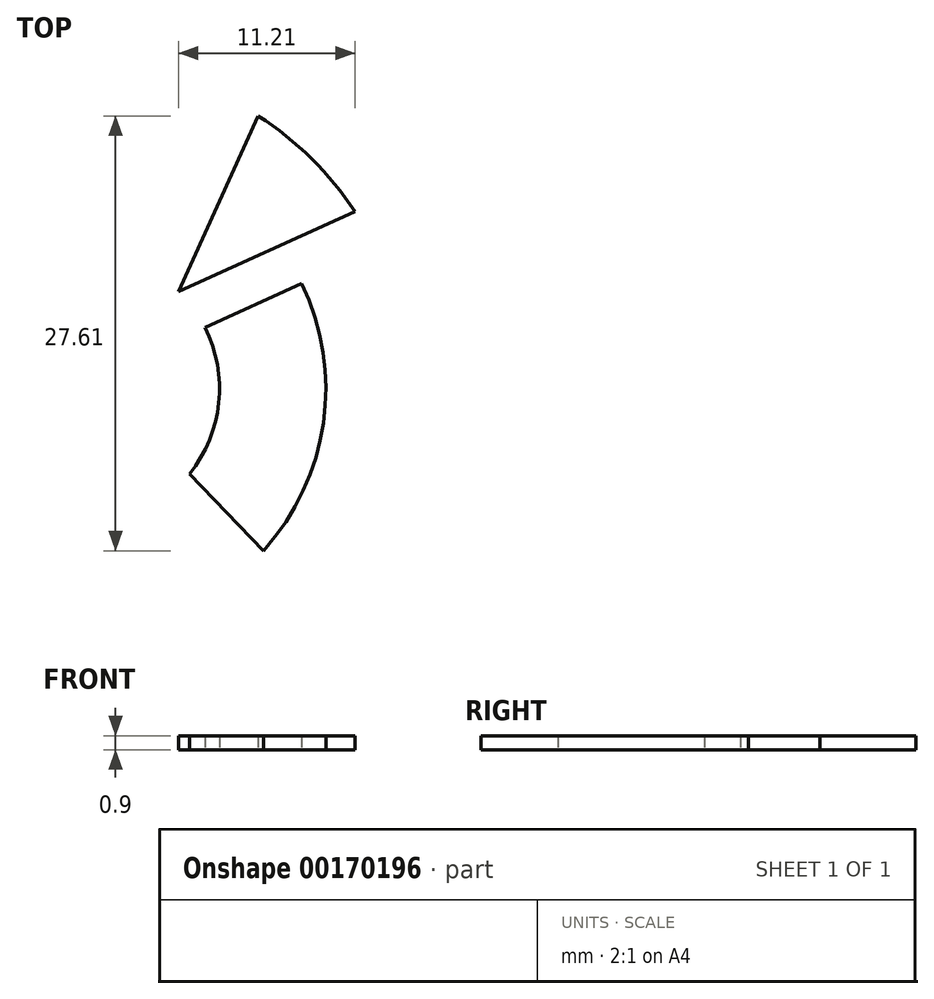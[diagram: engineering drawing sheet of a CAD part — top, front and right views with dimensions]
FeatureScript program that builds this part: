
annotation { "Feature Type Name" : "Feature", "Feature Type Description" : "" }
export const myFeature = defineFeature(function(context is Context, id is Id, definition is map)
    precondition{}
    {
        {
            var Q0;
            Q0=qCreatedBy(makeId("Top.planeOp"),FACE);
            var sketch = newSketch(context, id + "F0", { "sketchPlane" : qUnion([Q0])});
            skCircle(sketch, "E0", {"center": v(0, 0) * mm, "radius": 20 * mm});
            skCircle(sketch, "E1", {"center": v(0, 0) * mm, "radius": 13.35 * mm});
            skCircle(sketch, "E2", {"center": v(0, 0) * mm, "radius": 4.06 * mm});
            skCircle(sketch, "E3", {"center": v(0, 0) * mm, "radius": 10.58 * mm});
            skCircle(sketch, "E4", {"center": v(0, 0) * mm, "radius": 8.61 * mm});
            skCircle(sketch, "E5", {"center": v(0, 0) * mm, "radius": 15.36 * mm});
            skCircle(sketch, "E6", {"center": v(0, 0) * mm, "radius": 20.56 * mm});
            skCircle(sketch, "E7", {"center": v(0, 21.5) * mm, "radius": 3.37 * mm});
            skCircle(sketch, "E8", {"center": v(0, 22.43) * mm, "radius": 1.5 * mm});
            skLineSegment(sketch, "E9", {"start": v(6, 6.18) * mm, "end": v(11.07, 17.32) * mm});
            skLineSegment(sketch, "E10", {"start": v(6, 6.18) * mm, "end": v(17.22, 11.24) * mm});
            skLineSegment(sketch, "E11", {"start": v(8.19, 18.25) * mm, "end": v(1.98, 3.54) * mm});
            skLineSegment(sketch, "E12", {"start": v(1.66, -3.7) * mm, "end": v(12.41, -15.68) * mm});
            skLineSegment(sketch, "E13", {"start": v(7.68, 3.9) * mm, "end": v(13.83, 6.68) * mm});
            skLineSegment(sketch, "E14", {"start": v(11.4, -10.3) * mm, "end": v(6.71, -5.4) * mm});
            skSolve(sketch);
        }
        {
            var Q0;
            {var subQ1=sQuery(id+"F0.wireOp",EDGE,"E0");var subQ4=sQuery(id+"F0.wireOp",EDGE,"E11");var subQ10=makeQuery(id+"F0.imprint","INTERSECT",VERTEX,{"derivedFrom":[subQ1,subQ4]});Q0=makeQuery(id+"F0.imprint","IMPRINT",FACE,{"disambiguationData":[TD([[makeQuery(id+"F0.imprint","IMPRINT",EDGE,{"disambiguationData":[TD([[subQ10,-1.0]])],"derivedFrom":subQ1}),1.0]])]});}
            var Q1;
            {var subQ0=sQuery(id+"F0.wireOp",EDGE,"E11");var subQ1=sQuery(id+"F0.wireOp",EDGE,"E1");var subQ2=makeQuery(id+"F0.imprint","INTERSECT",VERTEX,{"derivedFrom":[subQ1,subQ0]});Q1=makeQuery(id+"F0.imprint","IMPRINT",FACE,{"disambiguationData":[TD([[makeQuery(id+"F0.imprint","IMPRINT",EDGE,{"disambiguationData":[TD([[subQ2,-1.0]])],"derivedFrom":subQ1}),-1.0]])]});}
            var Q2;
            {var subQ0=sQuery(id+"F0.wireOp",EDGE,"E11");var subQ1=sQuery(id+"F0.wireOp",EDGE,"E1");var subQ2=makeQuery(id+"F0.imprint","INTERSECT",VERTEX,{"derivedFrom":[subQ1,subQ0]});Q2=makeQuery(id+"F0.imprint","IMPRINT",FACE,{"disambiguationData":[TD([[makeQuery(id+"F0.imprint","IMPRINT",EDGE,{"disambiguationData":[TD([[subQ2,-1.0]])],"derivedFrom":subQ1}),1.0]])]});}
            var Q3;
            {var subQ0=sQuery(id+"F0.wireOp",EDGE,"E11");var subQ1=sQuery(id+"F0.wireOp",EDGE,"E3");var subQ2=makeQuery(id+"F0.imprint","INTERSECT",VERTEX,{"derivedFrom":[subQ1,subQ0]});Q3=makeQuery(id+"F0.imprint","IMPRINT",FACE,{"disambiguationData":[TD([[makeQuery(id+"F0.imprint","IMPRINT",EDGE,{"disambiguationData":[TD([[subQ2,-1.0]])],"derivedFrom":subQ1}),1.0]])]});}
            var Q4;
            {var subQ0=sQuery(id+"F0.wireOp",EDGE,"E11");var subQ1=sQuery(id+"F0.wireOp",EDGE,"E2");var subQ2=makeQuery(id+"F0.imprint","INTERSECT",VERTEX,{"derivedFrom":[subQ1,subQ0]});Q4=makeQuery(id+"F0.imprint","IMPRINT",FACE,{"disambiguationData":[TD([[makeQuery(id+"F0.imprint","IMPRINT",EDGE,{"disambiguationData":[TD([[subQ2,-1.0]])],"derivedFrom":subQ1}),-1.0]])]});}
            var Q5;
            {var subQ0=sQuery(id+"F0.wireOp",EDGE,"E7");var subQ1=sQuery(id+"F0.wireOp",EDGE,"E0");var subQ2=makeQuery(id+"F0.imprint","INTERSECT",VERTEX,{"disambiguationData":[OD(0.0)],"derivedFrom":[subQ1,subQ0]});Q5=makeQuery(id+"F0.imprint","IMPRINT",FACE,{"disambiguationData":[TD([[makeQuery(id+"F0.imprint","IMPRINT",EDGE,{"disambiguationData":[TD([[subQ2,-1.0]])],"derivedFrom":subQ1}),1.0]])]});}
            var Q6;
            {var subQ0=sQuery(id+"F0.wireOp",EDGE,"E7");var subQ1=sQuery(id+"F0.wireOp",EDGE,"E0");var subQ2=makeQuery(id+"F0.imprint","INTERSECT",VERTEX,{"disambiguationData":[OD(0.0)],"derivedFrom":[subQ1,subQ0]});Q6=makeQuery(id+"F0.imprint","IMPRINT",FACE,{"disambiguationData":[TD([[makeQuery(id+"F0.imprint","IMPRINT",EDGE,{"disambiguationData":[TD([[subQ2,-1.0]])],"derivedFrom":subQ1}),-1.0]])]});}
            var Q7;
            Q7=makeQuery(id+"F0.imprint","IMPRINT",FACE,{"disambiguationData":[TD([[makeQuery(id+"F0.imprint","IMPRINT",EDGE,{"derivedFrom":sQuery(id+"F0.wireOp",EDGE,"E8")}),-1.0]])]});
            var Q8;
            {var subQ0=sQuery(id+"F0.wireOp",EDGE,"E10");var subQ1=sQuery(id+"F0.wireOp",EDGE,"E1");var subQ2=makeQuery(id+"F0.imprint","INTERSECT",VERTEX,{"derivedFrom":[subQ1,subQ0]});Q8=makeQuery(id+"F0.imprint","IMPRINT",FACE,{"disambiguationData":[TD([[makeQuery(id+"F0.imprint","IMPRINT",EDGE,{"disambiguationData":[TD([[subQ2,1.0]])],"derivedFrom":subQ1}),-1.0]])]});}
            var Q9;
            {var subQ0=sQuery(id+"F0.wireOp",EDGE,"E10");var subQ1=sQuery(id+"F0.wireOp",EDGE,"E1");var subQ2=makeQuery(id+"F0.imprint","INTERSECT",VERTEX,{"derivedFrom":[subQ1,subQ0]});Q9=makeQuery(id+"F0.imprint","IMPRINT",FACE,{"disambiguationData":[TD([[makeQuery(id+"F0.imprint","IMPRINT",EDGE,{"disambiguationData":[TD([[subQ2,1.0]])],"derivedFrom":subQ1}),1.0]])]});}
            var Q10;
            {var subQ0=sQuery(id+"F0.wireOp",EDGE,"E10");var subQ1=sQuery(id+"F0.wireOp",EDGE,"E3");var subQ2=makeQuery(id+"F0.imprint","INTERSECT",VERTEX,{"derivedFrom":[subQ1,subQ0]});Q10=makeQuery(id+"F0.imprint","IMPRINT",FACE,{"disambiguationData":[TD([[makeQuery(id+"F0.imprint","IMPRINT",EDGE,{"disambiguationData":[TD([[subQ2,1.0]])],"derivedFrom":subQ1}),1.0]])]});}
            var Q11;
            {var subQ0=sQuery(id+"F0.wireOp",EDGE,"E9");var subQ1=sQuery(id+"F0.wireOp",EDGE,"E3");var subQ2=makeQuery(id+"F0.imprint","INTERSECT",VERTEX,{"derivedFrom":[subQ1,subQ0]});Q11=makeQuery(id+"F0.imprint","IMPRINT",FACE,{"disambiguationData":[TD([[makeQuery(id+"F0.imprint","IMPRINT",EDGE,{"disambiguationData":[TD([[subQ2,1.0]])],"derivedFrom":subQ1}),1.0]])]});}
            var Q12;
            {var subQ0=sQuery(id+"F0.wireOp",EDGE,"E9");var subQ1=sQuery(id+"F0.wireOp",EDGE,"E3");var subQ2=makeQuery(id+"F0.imprint","INTERSECT",VERTEX,{"derivedFrom":[subQ1,subQ0]});Q12=makeQuery(id+"F0.imprint","IMPRINT",FACE,{"disambiguationData":[TD([[makeQuery(id+"F0.imprint","IMPRINT",EDGE,{"disambiguationData":[TD([[subQ2,-1.0]])],"derivedFrom":subQ1}),1.0]])]});}
            var Q13;
            {var subQ0=sQuery(id+"F0.wireOp",EDGE,"E9");var subQ1=sQuery(id+"F0.wireOp",EDGE,"E1");var subQ2=makeQuery(id+"F0.imprint","INTERSECT",VERTEX,{"derivedFrom":[subQ1,subQ0]});Q13=makeQuery(id+"F0.imprint","IMPRINT",FACE,{"disambiguationData":[TD([[makeQuery(id+"F0.imprint","IMPRINT",EDGE,{"disambiguationData":[TD([[subQ2,-1.0]])],"derivedFrom":subQ1}),1.0]])]});}
            var Q14;
            {var subQ0=sQuery(id+"F0.wireOp",EDGE,"E9");var subQ1=sQuery(id+"F0.wireOp",EDGE,"E1");var subQ2=makeQuery(id+"F0.imprint","INTERSECT",VERTEX,{"derivedFrom":[subQ1,subQ0]});Q14=makeQuery(id+"F0.imprint","IMPRINT",FACE,{"disambiguationData":[TD([[makeQuery(id+"F0.imprint","IMPRINT",EDGE,{"disambiguationData":[TD([[subQ2,-1.0]])],"derivedFrom":subQ1}),-1.0]])]});}
            var Q15;
            {var subQ0=sQuery(id+"F0.wireOp",EDGE,"E9");var subQ1=sQuery(id+"F0.wireOp",EDGE,"E1");var subQ2=makeQuery(id+"F0.imprint","INTERSECT",VERTEX,{"derivedFrom":[subQ1,subQ0]});Q15=makeQuery(id+"F0.imprint","IMPRINT",FACE,{"disambiguationData":[TD([[makeQuery(id+"F0.imprint","IMPRINT",EDGE,{"disambiguationData":[TD([[subQ2,1.0]])],"derivedFrom":subQ1}),1.0]])]});}
            var Q16;
            {var subQ0=sQuery(id+"F0.wireOp",EDGE,"E9");var subQ1=sQuery(id+"F0.wireOp",EDGE,"E1");var subQ2=makeQuery(id+"F0.imprint","INTERSECT",VERTEX,{"derivedFrom":[subQ1,subQ0]});Q16=makeQuery(id+"F0.imprint","IMPRINT",FACE,{"disambiguationData":[TD([[makeQuery(id+"F0.imprint","IMPRINT",EDGE,{"disambiguationData":[TD([[subQ2,1.0]])],"derivedFrom":subQ1}),-1.0]])]});}
            var Q17;
            {var subQ0=sQuery(id+"F0.wireOp",EDGE,"E9");var subQ1=sQuery(id+"F0.wireOp",EDGE,"E0");var subQ2=makeQuery(id+"F0.imprint","INTERSECT",VERTEX,{"derivedFrom":[subQ1,subQ0]});Q17=makeQuery(id+"F0.imprint","IMPRINT",FACE,{"disambiguationData":[TD([[makeQuery(id+"F0.imprint","IMPRINT",EDGE,{"disambiguationData":[TD([[subQ2,1.0]])],"derivedFrom":subQ1}),1.0]])]});}
            var Q18;
            {var subQ0=sQuery(id+"F0.wireOp",EDGE,"E9");var subQ1=sQuery(id+"F0.wireOp",EDGE,"E0");var subQ2=makeQuery(id+"F0.imprint","INTERSECT",VERTEX,{"derivedFrom":[subQ1,subQ0]});Q18=makeQuery(id+"F0.imprint","IMPRINT",FACE,{"disambiguationData":[TD([[makeQuery(id+"F0.imprint","IMPRINT",EDGE,{"disambiguationData":[TD([[subQ2,1.0]])],"derivedFrom":subQ1}),-1.0]])]});}
            extrude(context, id + "F1", {"entities" : qUnion([Q0, Q1, Q2, Q3, Q4, Q5, Q6, Q7, Q8, Q9, Q10, Q11, Q12, Q13, Q14, Q15, Q16, Q17, Q18]), "oppositeDirection" : true, "depth" : 2.7 * mm});
        }
        {
            var Q0;
            {var subQ1=sQuery(id+"F0.wireOp",EDGE,"E0");var subQ4=sQuery(id+"F0.wireOp",EDGE,"E11");var subQ10=makeQuery(id+"F0.imprint","INTERSECT",VERTEX,{"derivedFrom":[subQ1,subQ4]});Q0=makeQuery(id+"F0.imprint","IMPRINT",FACE,{"disambiguationData":[TD([[makeQuery(id+"F0.imprint","IMPRINT",EDGE,{"disambiguationData":[TD([[subQ10,-1.0]])],"derivedFrom":subQ1}),1.0]])]});}
            var Q1;
            {var subQ0=sQuery(id+"F0.wireOp",EDGE,"E11");var subQ1=sQuery(id+"F0.wireOp",EDGE,"E1");var subQ2=makeQuery(id+"F0.imprint","INTERSECT",VERTEX,{"derivedFrom":[subQ1,subQ0]});Q1=makeQuery(id+"F0.imprint","IMPRINT",FACE,{"disambiguationData":[TD([[makeQuery(id+"F0.imprint","IMPRINT",EDGE,{"disambiguationData":[TD([[subQ2,-1.0]])],"derivedFrom":subQ1}),-1.0]])]});}
            var Q2;
            {var subQ0=sQuery(id+"F0.wireOp",EDGE,"E11");var subQ1=sQuery(id+"F0.wireOp",EDGE,"E3");var subQ2=makeQuery(id+"F0.imprint","INTERSECT",VERTEX,{"derivedFrom":[subQ1,subQ0]});Q2=makeQuery(id+"F0.imprint","IMPRINT",FACE,{"disambiguationData":[TD([[makeQuery(id+"F0.imprint","IMPRINT",EDGE,{"disambiguationData":[TD([[subQ2,-1.0]])],"derivedFrom":subQ1}),1.0]])]});}
            var Q3;
            {var subQ0=sQuery(id+"F0.wireOp",EDGE,"E11");var subQ1=sQuery(id+"F0.wireOp",EDGE,"E2");var subQ2=makeQuery(id+"F0.imprint","INTERSECT",VERTEX,{"derivedFrom":[subQ1,subQ0]});Q3=makeQuery(id+"F0.imprint","IMPRINT",FACE,{"disambiguationData":[TD([[makeQuery(id+"F0.imprint","IMPRINT",EDGE,{"disambiguationData":[TD([[subQ2,-1.0]])],"derivedFrom":subQ1}),-1.0]])]});}
            var Q4;
            {var subQ0=sQuery(id+"F0.wireOp",EDGE,"E7");var subQ1=sQuery(id+"F0.wireOp",EDGE,"E0");var subQ2=makeQuery(id+"F0.imprint","INTERSECT",VERTEX,{"disambiguationData":[OD(0.0)],"derivedFrom":[subQ1,subQ0]});Q4=makeQuery(id+"F0.imprint","IMPRINT",FACE,{"disambiguationData":[TD([[makeQuery(id+"F0.imprint","IMPRINT",EDGE,{"disambiguationData":[TD([[subQ2,-1.0]])],"derivedFrom":subQ1}),1.0]])]});}
            extrude(context, id + "F2", {"entities" : qUnion([Q0, Q1, Q2, Q3, Q4]), "operationType" : NewBodyOperationType.ADD, "depth" : 0.9 * mm});
        }
        {
            var Q0;
            {var subQ0=sQuery(id+"F0.wireOp",EDGE,"E13");var subQ1=sQuery(id+"F0.wireOp",EDGE,"E3");var subQ2=makeQuery(id+"F0.imprint","INTERSECT",VERTEX,{"derivedFrom":[subQ1,subQ0]});Q0=makeQuery(id+"F0.imprint","IMPRINT",FACE,{"disambiguationData":[TD([[makeQuery(id+"F0.imprint","IMPRINT",EDGE,{"disambiguationData":[TD([[subQ2,1.0]])],"derivedFrom":subQ1}),1.0]])]});}
            var Q1;
            {var subQ0=sQuery(id+"F0.wireOp",EDGE,"E13");var subQ1=sQuery(id+"F0.wireOp",EDGE,"E1");var subQ2=makeQuery(id+"F0.imprint","INTERSECT",VERTEX,{"derivedFrom":[subQ1,subQ0]});Q1=makeQuery(id+"F0.imprint","IMPRINT",FACE,{"disambiguationData":[TD([[makeQuery(id+"F0.imprint","IMPRINT",EDGE,{"disambiguationData":[TD([[subQ2,1.0]])],"derivedFrom":subQ1}),1.0]])]});}
            var Q2;
            {var subQ0=sQuery(id+"F0.wireOp",EDGE,"E13");var subQ1=sQuery(id+"F0.wireOp",EDGE,"E1");var subQ2=makeQuery(id+"F0.imprint","INTERSECT",VERTEX,{"derivedFrom":[subQ1,subQ0]});Q2=makeQuery(id+"F0.imprint","IMPRINT",FACE,{"disambiguationData":[TD([[makeQuery(id+"F0.imprint","IMPRINT",EDGE,{"disambiguationData":[TD([[subQ2,1.0]])],"derivedFrom":subQ1}),-1.0]])]});}
            var Q3;
            {var subQ0=sQuery(id+"F0.wireOp",EDGE,"E12");var subQ1=sQuery(id+"F0.wireOp",EDGE,"E1");var subQ2=makeQuery(id+"F0.imprint","INTERSECT",VERTEX,{"derivedFrom":[subQ1,subQ0]});Q3=makeQuery(id+"F0.imprint","IMPRINT",FACE,{"disambiguationData":[TD([[makeQuery(id+"F0.imprint","IMPRINT",EDGE,{"disambiguationData":[TD([[subQ2,-1.0]])],"derivedFrom":subQ1}),-1.0]])]});}
            var Q4;
            {var subQ0=sQuery(id+"F0.wireOp",EDGE,"E12");var subQ1=sQuery(id+"F0.wireOp",EDGE,"E1");var subQ2=makeQuery(id+"F0.imprint","INTERSECT",VERTEX,{"derivedFrom":[subQ1,subQ0]});Q4=makeQuery(id+"F0.imprint","IMPRINT",FACE,{"disambiguationData":[TD([[makeQuery(id+"F0.imprint","IMPRINT",EDGE,{"disambiguationData":[TD([[subQ2,-1.0]])],"derivedFrom":subQ1}),1.0]])]});}
            var Q5;
            {var subQ0=sQuery(id+"F0.wireOp",EDGE,"E12");var subQ1=sQuery(id+"F0.wireOp",EDGE,"E3");var subQ2=makeQuery(id+"F0.imprint","INTERSECT",VERTEX,{"derivedFrom":[subQ1,subQ0]});Q5=makeQuery(id+"F0.imprint","IMPRINT",FACE,{"disambiguationData":[TD([[makeQuery(id+"F0.imprint","IMPRINT",EDGE,{"disambiguationData":[TD([[subQ2,-1.0]])],"derivedFrom":subQ1}),1.0]])]});}
            extrude(context, id + "F3", {"entities" : qUnion([Q0, Q1, Q2, Q3, Q4, Q5]), "operationType" : NewBodyOperationType.ADD, "oppositeDirection" : true, "depth" : 2.7 * mm});
        }
        {
            var Q0;
            {var subQ0=sQuery(id+"F0.wireOp",EDGE,"E13");var subQ1=sQuery(id+"F0.wireOp",EDGE,"E1");var subQ2=makeQuery(id+"F0.imprint","INTERSECT",VERTEX,{"derivedFrom":[subQ1,subQ0]});Q0=makeQuery(id+"F0.imprint","IMPRINT",FACE,{"disambiguationData":[TD([[makeQuery(id+"F0.imprint","IMPRINT",EDGE,{"disambiguationData":[TD([[subQ2,1.0]])],"derivedFrom":subQ1}),-1.0]])]});}
            var Q1;
            {var subQ0=sQuery(id+"F0.wireOp",EDGE,"E13");var subQ1=sQuery(id+"F0.wireOp",EDGE,"E1");var subQ2=makeQuery(id+"F0.imprint","INTERSECT",VERTEX,{"derivedFrom":[subQ1,subQ0]});Q1=makeQuery(id+"F0.imprint","IMPRINT",FACE,{"disambiguationData":[TD([[makeQuery(id+"F0.imprint","IMPRINT",EDGE,{"disambiguationData":[TD([[subQ2,1.0]])],"derivedFrom":subQ1}),1.0]])]});}
            var Q2;
            {var subQ0=sQuery(id+"F0.wireOp",EDGE,"E13");var subQ1=sQuery(id+"F0.wireOp",EDGE,"E3");var subQ2=makeQuery(id+"F0.imprint","INTERSECT",VERTEX,{"derivedFrom":[subQ1,subQ0]});Q2=makeQuery(id+"F0.imprint","IMPRINT",FACE,{"disambiguationData":[TD([[makeQuery(id+"F0.imprint","IMPRINT",EDGE,{"disambiguationData":[TD([[subQ2,1.0]])],"derivedFrom":subQ1}),1.0]])]});}
            var Q3;
            {var subQ0=sQuery(id+"F0.wireOp",EDGE,"E9");var subQ1=sQuery(id+"F0.wireOp",EDGE,"E0");var subQ2=makeQuery(id+"F0.imprint","INTERSECT",VERTEX,{"derivedFrom":[subQ1,subQ0]});Q3=makeQuery(id+"F0.imprint","IMPRINT",FACE,{"disambiguationData":[TD([[makeQuery(id+"F0.imprint","IMPRINT",EDGE,{"disambiguationData":[TD([[subQ2,1.0]])],"derivedFrom":subQ1}),-1.0]])]});}
            var Q4;
            {var subQ0=sQuery(id+"F0.wireOp",EDGE,"E10");var subQ1=sQuery(id+"F0.wireOp",EDGE,"E3");var subQ2=makeQuery(id+"F0.imprint","INTERSECT",VERTEX,{"derivedFrom":[subQ1,subQ0]});Q4=makeQuery(id+"F0.imprint","IMPRINT",FACE,{"disambiguationData":[TD([[makeQuery(id+"F0.imprint","IMPRINT",EDGE,{"disambiguationData":[TD([[subQ2,-1.0]])],"derivedFrom":subQ1}),1.0]])]});}
            var Q5;
            {var subQ0=sQuery(id+"F0.wireOp",EDGE,"E10");var subQ1=sQuery(id+"F0.wireOp",EDGE,"E1");var subQ2=makeQuery(id+"F0.imprint","INTERSECT",VERTEX,{"derivedFrom":[subQ1,subQ0]});Q5=makeQuery(id+"F0.imprint","IMPRINT",FACE,{"disambiguationData":[TD([[makeQuery(id+"F0.imprint","IMPRINT",EDGE,{"disambiguationData":[TD([[subQ2,-1.0]])],"derivedFrom":subQ1}),1.0]])]});}
            var Q6;
            {var subQ0=sQuery(id+"F0.wireOp",EDGE,"E10");var subQ1=sQuery(id+"F0.wireOp",EDGE,"E1");var subQ2=makeQuery(id+"F0.imprint","INTERSECT",VERTEX,{"derivedFrom":[subQ1,subQ0]});Q6=makeQuery(id+"F0.imprint","IMPRINT",FACE,{"disambiguationData":[TD([[makeQuery(id+"F0.imprint","IMPRINT",EDGE,{"disambiguationData":[TD([[subQ2,-1.0]])],"derivedFrom":subQ1}),-1.0]])]});}
            var Q7;
            {var subQ0=sQuery(id+"F0.wireOp",EDGE,"E9");var subQ1=sQuery(id+"F0.wireOp",EDGE,"E0");var subQ2=makeQuery(id+"F0.imprint","INTERSECT",VERTEX,{"derivedFrom":[subQ1,subQ0]});Q7=makeQuery(id+"F0.imprint","IMPRINT",FACE,{"disambiguationData":[TD([[makeQuery(id+"F0.imprint","IMPRINT",EDGE,{"disambiguationData":[TD([[subQ2,1.0]])],"derivedFrom":subQ1}),1.0]])]});}
            extrude(context, id + "F4", {"entities" : qUnion([Q0, Q1, Q2, Q3, Q4, Q5, Q6, Q7]), "operationType" : NewBodyOperationType.ADD, "depth" : 0.9 * mm});
        }
        {
            var Q0;
            {var subQ0=sQuery(id+"F0.wireOp",EDGE,"E7");var subQ1=sQuery(id+"F0.wireOp",EDGE,"E0");Q0=makeQuery(id+"F1.opExtrude","SWEPT_EDGE",EDGE,{"disambiguationData":[OSD([subQ1,subQ0]),TDD([makeQuery(id+"F0.imprint","INTERSECT",VERTEX,{"disambiguationData":[OD(0.0)],"derivedFrom":[subQ1,subQ0]})])]});}
            var Q1;
            {var subQ0=sQuery(id+"F0.wireOp",EDGE,"E7");var subQ1=sQuery(id+"F0.wireOp",EDGE,"E0");Q1=makeQuery(id+"F1.opExtrude","SWEPT_EDGE",EDGE,{"disambiguationData":[OSD([subQ1,subQ0]),TDD([makeQuery(id+"F0.imprint","INTERSECT",VERTEX,{"disambiguationData":[OD(1.0)],"derivedFrom":[subQ1,subQ0]})])]});}
            fillet(context, id + "F5", {"entities" : qUnion([Q0, Q1]), "radius" : 3 * mm, "tangentPropagation" : true, "allowEdgeOverflow" : false});
        }
        {
            var Q0;
            Q0=makeQuery(id+"F4.opExtrude","CAP_FACE",FACE,{"disambiguationData":[OSD([sQuery(id+"F0.wireOp",EDGE,"E4"),sQuery(id+"F0.wireOp",EDGE,"E5"),sQuery(id+"F0.wireOp",EDGE,"E13"),sQuery(id+"F0.wireOp",EDGE,"E14")])],"isStart":false});
            var Q1;
            Q1=makeQuery(id+"F4.opExtrude","CAP_FACE",FACE,{"disambiguationData":[OSD([sQuery(id+"F0.wireOp",EDGE,"E6"),sQuery(id+"F0.wireOp",EDGE,"E9"),sQuery(id+"F0.wireOp",EDGE,"E10")])],"isStart":false});
            extrude(context, id + "F6", {"entities" : qUnion([Q0, Q1]), "depth" : .9 * mm});
        }
        {
            var Q0;
            Q0=makeQuery(id+"F1.opExtrude","SWEPT_BODY",BODY,{"disambiguationData":[OSD([sQuery(id+"F0.wireOp",EDGE,"E0"),sQuery(id+"F0.wireOp",EDGE,"E2"),sQuery(id+"F0.wireOp",EDGE,"E4"),sQuery(id+"F0.wireOp",EDGE,"E5"),sQuery(id+"F0.wireOp",EDGE,"E6"),sQuery(id+"F0.wireOp",EDGE,"E7"),sQuery(id+"F0.wireOp",EDGE,"E8"),sQuery(id+"F0.wireOp",EDGE,"E9"),sQuery(id+"F0.wireOp",EDGE,"E10"),sQuery(id+"F0.wireOp",EDGE,"E11"),sQuery(id+"F0.wireOp",EDGE,"E12"),sQuery(id+"F0.wireOp",EDGE,"E13")])]});
            deleteBodies(context, id + "F7", {"entities" : qUnion([Q0])});
        }
    });
